# Revit family: QSTE
name_source: partatom
category: Mechanical Equipment
revit_build: Autodesk Revit 2018 (Build: 20170223_1515(x64)
units: mm (PartAtom-declared; Revit-internal decimal feet)

## family parameters
Always vertical = Yes
Cut with Voids When Loaded = No
OmniClass Number = 23.75.00.00
OmniClass Title = Climate Control (HVAC)
Part Type = Normal
Room Calculation Point = No
Round Connector Dimension = Use Diameter
Shared = No
Work Plane-Based = No

## types (56) — shared parameters
DUCT-FLANGE = 0' - 1"
Description = SERIES ELECTRIC HEAT
ESTH-depth = 0' - 8"
ESTH-flange = 0' - 0 3/4"
ESTH-offset = 0' - 6 1/2"
EnclHdim = 0' - 6 1/2"
EnclLdim = 1' - 10 1/4"
EnclOffset = 0' - 4 1/2"
EnclWdim = 0' - 11 1/8"
Inlet S = 0' - 5 1/2"
Inlet-offset = 0' - 4"
Manufacturer = ANEMOSTAT
Model = QSTE

## per-type parameters (varying)
- QSTE-1/4-HP-10L-S/ELBOW: BoX H=1' - 6"; Box H=1' - 6"; Box L=3' - 0"; Box W=2' - 8"; DUCT-C=1' - 0"; DUCT-D=1' - 4"; Discharge Height Y=0' - 11"; Discharge Width X=0' - 11 1/2"; Discharge for LH=Yes; Discharge for RH=No; ESTH for LH=Yes; ESTH for RH=No; ESTH-OAH=1' - 0 1/2"; ESTH-OAW=1' - 9 3/4"; Enclosure for LH=Yes; Enclosure for RH=No; Induction for LH=No; Induction for RH=No; Inlet Dia=0' - 9 7/8"; Inlet Radius=0' - 4 15/16"; Inlet for LH=Yes; Inlet for RH=No; Power Connect for LH=Yes; Power Connect for RH=No; Q5A=1' - 6"; Q5B=1' - 6"; Q5Q=1' - 6"; QSTE Discharge Offset=0' - 4 1/2"; Sound Elbow for LH=Yes; Sound Elbow for RH=No
- QSTE-1/2-HP-12L-S/ELBOW: BoX H=1' - 6"; Box H=1' - 6"; Box L=3' - 4"; Box W=3' - 4"; DUCT-C=1' - 5"; DUCT-D=1' - 4"; Discharge Height Y=1' - 0"; Discharge Width X=1' - 2"; Discharge for LH=Yes; Discharge for RH=No; ESTH for LH=Yes; ESTH for RH=No; ESTH-OAH=1' - 1 1/2"; ESTH-OAW=2' - 0 1/4"; Enclosure for LH=Yes; Enclosure for RH=No; Induction for LH=No; Induction for RH=No; Inlet Dia=0' - 11 7/8"; Inlet Radius=0' - 5 15/16"; Inlet for LH=Yes; Inlet for RH=No; Power Connect for LH=Yes; Power Connect for RH=No; Q5A=1' - 6"; Q5B=1' - 8"; Q5Q=1' - 6"; QSTE Discharge Offset=0' - 4 1/2"; Sound Elbow for LH=Yes; Sound Elbow for RH=No
- QSTE-1/2-HP-14L-S/ELBOW: BoX H=1' - 6"; Box H=1' - 6"; Box L=3' - 4"; Box W=3' - 4"; DUCT-C=1' - 5"; DUCT-D=1' - 4"; Discharge Height Y=1' - 0"; Discharge Width X=1' - 2"; Discharge for LH=Yes; Discharge for RH=No; ESTH for LH=Yes; ESTH for RH=No; ESTH-OAH=1' - 1 1/2"; ESTH-OAW=2' - 0 1/4"; Enclosure for LH=Yes; Enclosure for RH=No; Induction for LH=No; Induction for RH=No; Inlet Dia=1' - 1 7/8"; Inlet Radius=0' - 6 15/16"; Inlet for LH=Yes; Inlet for RH=No; Power Connect for LH=Yes; Power Connect for RH=No; Q5A=1' - 6"; Q5B=1' - 8"; Q5Q=1' - 6"; QSTE Discharge Offset=0' - 4 1/2"; Sound Elbow for LH=Yes; Sound Elbow for RH=No
- QSTE-3/4-HP-12L-S/ELBOW: BoX H=1' - 8"; Box H=1' - 8"; Box L=4' - 0"; Box W=4' - 0"; DUCT-C=1' - 9"; DUCT-D=1' - 6"; Discharge Height Y=1' - 4"; Discharge Width X=1' - 7"; Discharge for LH=Yes; Discharge for RH=No; ESTH for LH=Yes; ESTH for RH=No; ESTH-OAH=1' - 5 1/2"; ESTH-OAW=2' - 5 1/4"; Enclosure for LH=Yes; Enclosure for RH=No; Induction for LH=No; Induction for RH=No; Inlet Dia=0' - 11 7/8"; Inlet Radius=0' - 5 15/16"; Inlet for LH=Yes; Inlet for RH=No; Power Connect for LH=Yes; Power Connect for RH=No; Q5A=1' - 8"; Q5B=2' - 0"; Q5Q=1' - 8"; QSTE Discharge Offset=0' - 4 1/2"; Sound Elbow for LH=Yes; Sound Elbow for RH=No
- QSTE-3/4-HP-14L-S/ELBOW: BoX H=1' - 8"; Box H=1' - 8"; Box L=4' - 0"; Box W=4' - 0"; DUCT-C=1' - 9"; DUCT-D=1' - 6"; Discharge Height Y=1' - 4"; Discharge Width X=1' - 7"; Discharge for LH=Yes; Discharge for RH=No; ESTH for LH=Yes; ESTH for RH=No; ESTH-OAH=1' - 5 1/2"; ESTH-OAW=2' - 5 1/4"; Enclosure for LH=Yes; Enclosure for RH=No; Induction for LH=No; Induction for RH=No; Inlet Dia=1' - 1 7/8"; Inlet Radius=0' - 6 15/16"; Inlet for LH=Yes; Inlet for RH=No; Power Connect for LH=Yes; Power Connect for RH=No; Q5A=1' - 8"; Q5B=2' - 0"; Q5Q=1' - 8"; QSTE Discharge Offset=0' - 4 1/2"; Sound Elbow for LH=Yes; Sound Elbow for RH=No
- QSTE-1-HP-12L-S/ELBOW: BoX H=1' - 8"; Box H=1' - 8"; Box L=4' - 0"; Box W=4' - 0"; DUCT-C=1' - 9"; DUCT-D=1' - 6"; Discharge Height Y=1' - 4"; Discharge Width X=1' - 7"; Discharge for LH=Yes; Discharge for RH=No; ESTH for LH=Yes; ESTH for RH=No; ESTH-OAH=1' - 5 1/2"; ESTH-OAW=2' - 5 1/4"; Enclosure for LH=No; Enclosure for RH=Yes; Induction for LH=No; Induction for RH=No; Inlet Dia=0' - 11 7/8"; Inlet Radius=0' - 5 15/16"; Inlet for LH=Yes; Inlet for RH=No; Power Connect for LH=Yes; Power Connect for RH=No; Q5A=1' - 8"; Q5B=2' - 0"; Q5Q=1' - 8"; QSTE Discharge Offset=0' - 4 1/2"; Sound Elbow for LH=Yes; Sound Elbow for RH=No
- QSTE-1-HP-14L-W/OUT S/ELBOW: BoX H=1' - 8"; Box H=1' - 8"; Box L=4' - 0"; Box W=4' - 0"; DUCT-C=1' - 9"; DUCT-D=1' - 6"; Discharge Height Y=1' - 4"; Discharge Width X=1' - 7"; Discharge for LH=Yes; Discharge for RH=No; ESTH for LH=Yes; ESTH for RH=No; ESTH-OAH=1' - 5 1/2"; ESTH-OAW=2' - 5 1/4"; Enclosure for LH=Yes; Enclosure for RH=No; Induction for LH=Yes; Induction for RH=No; Inlet Dia=1' - 1 7/8"; Inlet Radius=0' - 6 15/16"; Inlet for LH=Yes; Inlet for RH=No; Power Connect for LH=Yes; Power Connect for RH=No; Q5A=1' - 8"; Q5B=2' - 0"; Q5Q=1' - 8"; QSTE Discharge Offset=0' - 4 1/2"; Sound Elbow for LH=No; Sound Elbow for RH=No
- QSTE-1-HP-16L-S/ELBOW: BoX H=1' - 8"; Box H=1' - 8"; Box L=4' - 0"; Box W=4' - 0"; DUCT-C=1' - 9"; DUCT-D=1' - 6"; Discharge Height Y=1' - 4"; Discharge Width X=1' - 7"; Discharge for LH=Yes; Discharge for RH=No; ESTH for LH=Yes; ESTH for RH=No; ESTH-OAH=1' - 5 1/2"; ESTH-OAW=2' - 5 1/4"; Enclosure for LH=Yes; Enclosure for RH=No; Induction for LH=No; Induction for RH=No; Inlet Dia=1' - 3 7/8"; Inlet Radius=0' - 7 15/16"; Inlet for LH=Yes; Inlet for RH=No; Power Connect for LH=Yes; Power Connect for RH=No; Q5A=1' - 8"; Q5B=2' - 0"; Q5Q=1' - 8"; QSTE Discharge Offset=0' - 4 1/2"; Sound Elbow for LH=Yes; Sound Elbow for RH=No
- QSTE-1/2-HP-10R-S/ELBOW: BoX H=1' - 6"; Box H=1' - 6"; Box L=3' - 4"; Box W=3' - 4"; DUCT-C=1' - 5"; DUCT-D=1' - 4"; Discharge Height Y=1' - 0"; Discharge Width X=1' - 2"; Discharge for LH=No; Discharge for RH=Yes; ESTH for LH=No; ESTH for RH=Yes; ESTH-OAH=1' - 1 1/2"; ESTH-OAW=2' - 0 1/4"; Enclosure for LH=No; Enclosure for RH=Yes; Induction for LH=No; Induction for RH=No; Inlet Dia=0' - 9 7/8"; Inlet Radius=0' - 4 15/16"; Inlet for LH=No; Inlet for RH=Yes; Power Connect for LH=No; Power Connect for RH=Yes; Q5A=1' - 6"; Q5B=1' - 8"; Q5Q=1' - 6"; QSTE Discharge Offset=0' - 4 1/2"; Sound Elbow for LH=No; Sound Elbow for RH=Yes
- QSTE-1/2-HP-12R-S/ELBOW: BoX H=1' - 6"; Box H=1' - 6"; Box L=3' - 4"; Box W=3' - 4"; DUCT-C=1' - 5"; DUCT-D=1' - 4"; Discharge Height Y=1' - 0"; Discharge Width X=1' - 2"; Discharge for LH=No; Discharge for RH=Yes; ESTH for LH=No; ESTH for RH=Yes; ESTH-OAH=1' - 1 1/2"; ESTH-OAW=2' - 0 1/4"; Enclosure for LH=No; Enclosure for RH=Yes; Induction for LH=No; Induction for RH=No; Inlet Dia=0' - 11 7/8"; Inlet Radius=0' - 5 15/16"; Inlet for LH=No; Inlet for RH=Yes; Power Connect for LH=No; Power Connect for RH=Yes; Q5A=1' - 6"; Q5B=1' - 8"; Q5Q=1' - 6"; QSTE Discharge Offset=0' - 4 1/2"; Sound Elbow for LH=No; Sound Elbow for RH=Yes
- QSTE-1/2-HP-14R-S/ELBOW: BoX H=1' - 6"; Box H=1' - 6"; Box L=3' - 4"; Box W=3' - 4"; DUCT-C=1' - 5"; DUCT-D=1' - 4"; Discharge Height Y=1' - 0"; Discharge Width X=1' - 2"; Discharge for LH=No; Discharge for RH=Yes; ESTH for LH=No; ESTH for RH=Yes; ESTH-OAH=1' - 1 1/2"; ESTH-OAW=2' - 0 1/4"; Enclosure for LH=No; Enclosure for RH=Yes; Induction for LH=No; Induction for RH=No; Inlet Dia=1' - 1 7/8"; Inlet Radius=0' - 6 15/16"; Inlet for LH=No; Inlet for RH=Yes; Power Connect for LH=No; Power Connect for RH=Yes; Q5A=1' - 6"; Q5B=1' - 8"; Q5Q=1' - 6"; QSTE Discharge Offset=0' - 4 1/2"; Sound Elbow for LH=No; Sound Elbow for RH=Yes
- QSTE-1/4-HP-10R-S/ELBOW: BoX H=1' - 6"; Box H=1' - 6"; Box L=3' - 0"; Box W=2' - 8"; DUCT-C=1' - 0"; DUCT-D=1' - 4"; Discharge Height Y=0' - 11"; Discharge Width X=0' - 11 1/2"; Discharge for LH=No; Discharge for RH=Yes; ESTH for LH=No; ESTH for RH=Yes; ESTH-OAH=1' - 0 1/2"; ESTH-OAW=1' - 9 3/4"; Enclosure for LH=No; Enclosure for RH=No; Induction for LH=No; Induction for RH=No; Inlet Dia=0' - 9 7/8"; Inlet Radius=0' - 4 15/16"; Inlet for LH=No; Inlet for RH=Yes; Power Connect for LH=No; Power Connect for RH=Yes; Q5A=1' - 6"; Q5B=1' - 6"; Q5Q=1' - 6"; QSTE Discharge Offset=0' - 4 1/2"; Sound Elbow for LH=No; Sound Elbow for RH=Yes
- QSTE-1-HP-12R-W/OUT S/ELBOW: BoX H=1' - 8"; Box H=1' - 8"; Box L=4' - 0"; Box W=4' - 0"; DUCT-C=1' - 9"; DUCT-D=1' - 6"; Discharge Height Y=1' - 4"; Discharge Width X=1' - 7"; Discharge for LH=No; Discharge for RH=Yes; ESTH for LH=No; ESTH for RH=Yes; ESTH-OAH=1' - 5 1/2"; ESTH-OAW=2' - 5 1/4"; Enclosure for LH=No; Enclosure for RH=Yes; Induction for LH=No; Induction for RH=Yes; Inlet Dia=0' - 11 7/8"; Inlet Radius=0' - 5 15/16"; Inlet for LH=No; Inlet for RH=Yes; Power Connect for LH=No; Power Connect for RH=Yes; Q5A=1' - 8"; Q5B=2' - 0"; Q5Q=1' - 8"; QSTE Discharge Offset=0' - 4 1/2"; Sound Elbow for LH=No; Sound Elbow for RH=No
- QSTE-1-HP-14R-S/ELBOW: BoX H=1' - 8"; Box H=1' - 8"; Box L=4' - 0"; Box W=4' - 0"; DUCT-C=1' - 9"; DUCT-D=1' - 6"; Discharge Height Y=1' - 4"; Discharge Width X=1' - 7"; Discharge for LH=No; Discharge for RH=Yes; ESTH for LH=No; ESTH for RH=Yes; ESTH-OAH=1' - 5 1/2"; ESTH-OAW=2' - 5 1/4"; Enclosure for LH=No; Enclosure for RH=Yes; Induction for LH=No; Induction for RH=No; Inlet Dia=1' - 1 7/8"; Inlet Radius=0' - 6 15/16"; Inlet for LH=No; Inlet for RH=Yes; Power Connect for LH=No; Power Connect for RH=Yes; Q5A=1' - 8"; Q5B=2' - 0"; Q5Q=1' - 8"; QSTE Discharge Offset=0' - 4 1/2"; Sound Elbow for LH=No; Sound Elbow for RH=Yes
- QSTE-1-HP-16R-S/ELBOW: BoX H=1' - 8"; Box H=1' - 8"; Box L=4' - 0"; Box W=4' - 0"; DUCT-C=1' - 9"; DUCT-D=1' - 6"; Discharge Height Y=1' - 4"; Discharge Width X=1' - 7"; Discharge for LH=No; Discharge for RH=Yes; ESTH for LH=No; ESTH for RH=Yes; ESTH-OAH=1' - 5 1/2"; ESTH-OAW=2' - 5 1/4"; Enclosure for LH=No; Enclosure for RH=Yes; Induction for LH=No; Induction for RH=No; Inlet Dia=1' - 3 7/8"; Inlet Radius=0' - 7 15/16"; Inlet for LH=No; Inlet for RH=Yes; Power Connect for LH=No; Power Connect for RH=Yes; Q5A=1' - 8"; Q5B=2' - 0"; Q5Q=1' - 8"; QSTE Discharge Offset=0' - 4 1/2"; Sound Elbow for LH=No; Sound Elbow for RH=Yes
- QSTE-3/4-HP-12R-S/ELBOW: BoX H=1' - 8"; Box H=1' - 8"; Box L=4' - 0"; Box W=4' - 0"; DUCT-C=1' - 9"; DUCT-D=1' - 6"; Discharge Height Y=1' - 4"; Discharge Width X=1' - 7"; Discharge for LH=No; Discharge for RH=Yes; ESTH for LH=No; ESTH for RH=Yes; ESTH-OAH=1' - 5 1/2"; ESTH-OAW=2' - 5 1/4"; Enclosure for LH=No; Enclosure for RH=Yes; Induction for LH=No; Induction for RH=No; Inlet Dia=0' - 11 7/8"; Inlet Radius=0' - 5 15/16"; Inlet for LH=No; Inlet for RH=Yes; Power Connect for LH=No; Power Connect for RH=Yes; Q5A=1' - 8"; Q5B=2' - 0"; Q5Q=1' - 8"; QSTE Discharge Offset=0' - 4 1/2"; Sound Elbow for LH=No; Sound Elbow for RH=Yes
- QSTE-3/4-HP-14R-S/ELBOW: BoX H=1' - 8"; Box H=1' - 8"; Box L=4' - 0"; Box W=4' - 0"; DUCT-C=1' - 9"; DUCT-D=1' - 6"; Discharge Height Y=1' - 4"; Discharge Width X=1' - 7"; Discharge for LH=No; Discharge for RH=Yes; ESTH for LH=No; ESTH for RH=Yes; ESTH-OAH=1' - 5 1/2"; ESTH-OAW=2' - 5 1/4"; Enclosure for LH=No; Enclosure for RH=Yes; Induction for LH=No; Induction for RH=No; Inlet Dia=1' - 1 7/8"; Inlet Radius=0' - 6 15/16"; Inlet for LH=No; Inlet for RH=Yes; Power Connect for LH=No; Power Connect for RH=Yes; Q5A=1' - 8"; Q5B=2' - 0"; Q5Q=1' - 8"; QSTE Discharge Offset=0' - 4 1/2"; Sound Elbow for LH=No; Sound Elbow for RH=Yes
- QSTE-1/2-HP-10L-W/OUT S/ELBOW: BoX H=1' - 6"; Box H=1' - 6"; Box L=3' - 4"; Box W=3' - 4"; DUCT-C=1' - 5"; DUCT-D=1' - 4"; Discharge Height Y=1' - 0"; Discharge Width X=1' - 2"; Discharge for LH=Yes; Discharge for RH=No; ESTH for LH=Yes; ESTH for RH=No; ESTH-OAH=1' - 1 1/2"; ESTH-OAW=2' - 0 1/4"; Enclosure for LH=Yes; Enclosure for RH=No; Induction for LH=Yes; Induction for RH=No; Inlet Dia=0' - 9 7/8"; Inlet Radius=0' - 4 15/16"; Inlet for LH=Yes; Inlet for RH=No; Power Connect for LH=Yes; Power Connect for RH=No; Q5A=1' - 6"; Q5B=1' - 8"; Q5Q=1' - 6"; QSTE Discharge Offset=0' - 4 1/2"; Sound Elbow for LH=No; Sound Elbow for RH=No
- QSTE-1/2-HP-10R-W/OUT S/ELBOW: BoX H=1' - 6"; Box H=1' - 6"; Box L=3' - 4"; Box W=3' - 4"; DUCT-C=1' - 5"; DUCT-D=1' - 4"; Discharge Height Y=1' - 0"; Discharge Width X=1' - 2"; Discharge for LH=No; Discharge for RH=Yes; ESTH for LH=No; ESTH for RH=Yes; ESTH-OAH=1' - 1 1/2"; ESTH-OAW=2' - 0 1/4"; Enclosure for LH=No; Enclosure for RH=Yes; Induction for LH=No; Induction for RH=Yes; Inlet Dia=0' - 9 7/8"; Inlet Radius=0' - 4 15/16"; Inlet for LH=No; Inlet for RH=Yes; Power Connect for LH=No; Power Connect for RH=Yes; Q5A=1' - 6"; Q5B=1' - 8"; Q5Q=1' - 6"; QSTE Discharge Offset=0' - 4 1/2"; Sound Elbow for LH=No; Sound Elbow for RH=No
- QSTE-1/2-HP-12L-W/OUT S/ELBOW: BoX H=1' - 6"; Box H=1' - 6"; Box L=3' - 4"; Box W=3' - 4"; DUCT-C=1' - 5"; DUCT-D=1' - 4"; Discharge Height Y=1' - 0"; Discharge Width X=1' - 2"; Discharge for LH=Yes; Discharge for RH=No; ESTH for LH=Yes; ESTH for RH=No; ESTH-OAH=1' - 1 1/2"; ESTH-OAW=2' - 0 1/4"; Enclosure for LH=Yes; Enclosure for RH=No; Induction for LH=Yes; Induction for RH=No; Inlet Dia=0' - 11 7/8"; Inlet Radius=0' - 5 15/16"; Inlet for LH=Yes; Inlet for RH=No; Power Connect for LH=Yes; Power Connect for RH=No; Q5A=1' - 6"; Q5B=1' - 8"; Q5Q=1' - 6"; QSTE Discharge Offset=0' - 4 1/2"; Sound Elbow for LH=No; Sound Elbow for RH=No
- QSTE-1/2-HP-12R-W/OUT S/ELBOW: BoX H=1' - 6"; Box H=1' - 6"; Box L=3' - 4"; Box W=3' - 4"; DUCT-C=1' - 5"; DUCT-D=1' - 4"; Discharge Height Y=1' - 0"; Discharge Width X=1' - 2"; Discharge for LH=No; Discharge for RH=Yes; ESTH for LH=No; ESTH for RH=Yes; ESTH-OAH=1' - 1 1/2"; ESTH-OAW=2' - 0 1/4"; Enclosure for LH=No; Enclosure for RH=Yes; Induction for LH=No; Induction for RH=Yes; Inlet Dia=0' - 11 7/8"; Inlet Radius=0' - 5 15/16"; Inlet for LH=No; Inlet for RH=Yes; Power Connect for LH=No; Power Connect for RH=Yes; Q5A=1' - 6"; Q5B=1' - 8"; Q5Q=1' - 6"; QSTE Discharge Offset=0' - 4 1/2"; Sound Elbow for LH=No; Sound Elbow for RH=No
- QSTE-1/2-HP-14L-W/OUT S/ELBOW: BoX H=1' - 6"; Box H=1' - 6"; Box L=3' - 4"; Box W=3' - 4"; DUCT-C=1' - 5"; DUCT-D=1' - 4"; Discharge Height Y=1' - 0"; Discharge Width X=1' - 2"; Discharge for LH=Yes; Discharge for RH=No; ESTH for LH=Yes; ESTH for RH=No; ESTH-OAH=1' - 1 1/2"; ESTH-OAW=2' - 0 1/4"; Enclosure for LH=Yes; Enclosure for RH=No; Induction for LH=Yes; Induction for RH=No; Inlet Dia=1' - 1 7/8"; Inlet Radius=0' - 6 15/16"; Inlet for LH=Yes; Inlet for RH=No; Power Connect for LH=Yes; Power Connect for RH=No; Q5A=1' - 6"; Q5B=1' - 8"; Q5Q=1' - 6"; QSTE Discharge Offset=0' - 4 1/2"; Sound Elbow for LH=No; Sound Elbow for RH=No
- QSTE-1/2-HP-14R-W/OUT S/ELBOW: BoX H=1' - 6"; Box H=1' - 6"; Box L=3' - 4"; Box W=3' - 4"; DUCT-C=1' - 5"; DUCT-D=1' - 4"; Discharge Height Y=1' - 0"; Discharge Width X=1' - 2"; Discharge for LH=No; Discharge for RH=Yes; ESTH for LH=No; ESTH for RH=Yes; ESTH-OAH=1' - 1 1/2"; ESTH-OAW=2' - 0 1/4"; Enclosure for LH=No; Enclosure for RH=Yes; Induction for LH=No; Induction for RH=Yes; Inlet Dia=1' - 1 7/8"; Inlet Radius=0' - 6 15/16"; Inlet for LH=No; Inlet for RH=Yes; Power Connect for LH=No; Power Connect for RH=Yes; Q5A=1' - 6"; Q5B=1' - 8"; Q5Q=1' - 6"; QSTE Discharge Offset=0' - 4 1/2"; Sound Elbow for LH=No; Sound Elbow for RH=No
- QSTE-1/6-HP-6R-W/OUT S/ELBOW: BoX H=1' - 6"; Box H=1' - 6"; Box L=3' - 0"; Box W=2' - 8"; DUCT-C=1' - 5"; DUCT-D=1' - 4"; Discharge Height Y=0' - 11"; Discharge Width X=0' - 11 1/2"; Discharge for LH=No; Discharge for RH=Yes; ESTH for LH=No; ESTH for RH=Yes; ESTH-OAH=1' - 0 1/2"; ESTH-OAW=1' - 9 3/4"; Enclosure for LH=No; Enclosure for RH=Yes; Induction for LH=No; Induction for RH=Yes; Inlet Dia=0' - 5 7/8"; Inlet Radius=0' - 2 15/16"; Inlet for LH=No; Inlet for RH=Yes; Power Connect for LH=No; Power Connect for RH=Yes; Q5A=1' - 6"; Q5B=1' - 6"; Q5Q=1' - 6"; QSTE Discharge Offset=0' - 4 1/2"; Sound Elbow for LH=No; Sound Elbow for RH=No
- QSTE-1/6-HP-7R-W/OUT S/ELBOW: BoX H=1' - 6"; Box H=1' - 6"; Box L=3' - 0"; Box W=2' - 8"; DUCT-C=1' - 0"; DUCT-D=1' - 4"; Discharge Height Y=0' - 11"; Discharge Width X=0' - 11 1/2"; Discharge for LH=No; Discharge for RH=Yes; ESTH for LH=No; ESTH for RH=Yes; ESTH-OAH=1' - 0 1/2"; ESTH-OAW=1' - 9 3/4"; Enclosure for LH=No; Enclosure for RH=Yes; Induction for LH=No; Induction for RH=Yes; Inlet Dia=0' - 6 7/8"; Inlet Radius=0' - 3 7/16"; Inlet for LH=No; Inlet for RH=Yes; Power Connect for LH=No; Power Connect for RH=Yes; Q5A=1' - 6"; Q5B=1' - 6"; Q5Q=1' - 6"; QSTE Discharge Offset=0' - 4 1/2"; Sound Elbow for LH=No; Sound Elbow for RH=No
- QSTE-1/6-HP-8R-W/OUT S/ELBOW: BoX H=1' - 6"; Box H=1' - 6"; Box L=3' - 0"; Box W=2' - 8"; DUCT-C=1' - 0"; DUCT-D=1' - 4"; Discharge Height Y=0' - 11"; Discharge Width X=0' - 11 1/2"; Discharge for LH=No; Discharge for RH=Yes; ESTH for LH=No; ESTH for RH=Yes; ESTH-OAH=1' - 0 1/2"; ESTH-OAW=1' - 9 3/4"; Enclosure for LH=No; Enclosure for RH=Yes; Induction for LH=No; Induction for RH=Yes; Inlet Dia=0' - 7 7/8"; Inlet Radius=0' - 3 15/16"; Inlet for LH=No; Inlet for RH=Yes; Power Connect for LH=No; Power Connect for RH=Yes; Q5A=1' - 6"; Q5B=1' - 6"; Q5Q=1' - 6"; QSTE Discharge Offset=0' - 4 1/2"; Sound Elbow for LH=No; Sound Elbow for RH=No
- QSTE-1/6-HP-8L-W/OUT S/ELBOW: BoX H=1' - 6"; Box H=1' - 6"; Box L=3' - 0"; Box W=2' - 8"; DUCT-C=1' - 0"; DUCT-D=1' - 4"; Discharge Height Y=0' - 11"; Discharge Width X=0' - 11 1/2"; Discharge for LH=Yes; Discharge for RH=No; ESTH for LH=Yes; ESTH for RH=No; ESTH-OAH=1' - 0 1/2"; ESTH-OAW=1' - 9 3/4"; Enclosure for LH=Yes; Enclosure for RH=No; Induction for LH=Yes; Induction for RH=No; Inlet Dia=0' - 7 7/8"; Inlet Radius=0' - 3 15/16"; Inlet for LH=Yes; Inlet for RH=No; Power Connect for LH=Yes; Power Connect for RH=No; Q5A=1' - 6"; Q5B=1' - 6"; Q5Q=1' - 6"; QSTE Discharge Offset=0' - 4 1/2"; Sound Elbow for LH=No; Sound Elbow for RH=No
- QSTE-1/4-HP-9L-W/OUT S/ELBOW: BoX H=1' - 6"; Box H=1' - 6"; Box L=3' - 0"; Box W=2' - 8"; DUCT-C=1' - 0"; DUCT-D=1' - 4"; Discharge Height Y=0' - 11"; Discharge Width X=0' - 11 1/2"; Discharge for LH=Yes; Discharge for RH=No; ESTH for LH=Yes; ESTH for RH=No; ESTH-OAH=1' - 0 1/2"; ESTH-OAW=1' - 9 3/4"; Enclosure for LH=Yes; Enclosure for RH=No; Induction for LH=Yes; Induction for RH=No; Inlet Dia=0' - 8 7/8"; Inlet Radius=0' - 4 7/16"; Inlet for LH=Yes; Inlet for RH=No; Power Connect for LH=Yes; Power Connect for RH=No; Q5A=1' - 6"; Q5B=1' - 6"; Q5Q=1' - 6"; QSTE Discharge Offset=0' - 4 1/2"; Sound Elbow for LH=No; Sound Elbow for RH=No
- QSTE-1/4-HP-9R-W/OUT S/ELBOW: BoX H=1' - 6"; Box H=1' - 6"; Box L=3' - 0"; Box W=2' - 8"; DUCT-C=1' - 0"; DUCT-D=1' - 4"; Discharge Height Y=0' - 11"; Discharge Width X=0' - 11 1/2"; Discharge for LH=No; Discharge for RH=Yes; ESTH for LH=No; ESTH for RH=Yes; ESTH-OAH=1' - 0 1/2"; ESTH-OAW=1' - 9 3/4"; Enclosure for LH=No; Enclosure for RH=Yes; Induction for LH=No; Induction for RH=Yes; Inlet Dia=0' - 8 7/8"; Inlet Radius=0' - 4 7/16"; Inlet for LH=No; Inlet for RH=Yes; Power Connect for LH=No; Power Connect for RH=Yes; Q5A=1' - 6"; Q5B=1' - 6"; Q5Q=1' - 6"; QSTE Discharge Offset=0' - 4 1/2"; Sound Elbow for LH=No; Sound Elbow for RH=No
- QSTE-1/4-HP-10L-W/OUT S/ELBOW: BoX H=1' - 6"; Box H=1' - 6"; Box L=3' - 0"; Box W=2' - 8"; DUCT-C=1' - 0"; DUCT-D=1' - 4"; Discharge Height Y=0' - 11"; Discharge Width X=0' - 11 1/2"; Discharge for LH=Yes; Discharge for RH=No; ESTH for LH=Yes; ESTH for RH=No; ESTH-OAH=1' - 0 1/2"; ESTH-OAW=1' - 9 3/4"; Enclosure for LH=Yes; Enclosure for RH=No; Induction for LH=Yes; Induction for RH=No; Inlet Dia=0' - 9 7/8"; Inlet Radius=0' - 4 15/16"; Inlet for LH=Yes; Inlet for RH=No; Power Connect for LH=Yes; Power Connect for RH=No; Q5A=1' - 6"; Q5B=1' - 6"; Q5Q=1' - 6"; QSTE Discharge Offset=0' - 4 1/2"; Sound Elbow for LH=No; Sound Elbow for RH=No
- QSTE-1/4-HP-10R-W/OUT S/ELBOW: BoX H=1' - 6"; Box H=1' - 6"; Box L=3' - 0"; Box W=2' - 8"; DUCT-C=1' - 0"; DUCT-D=1' - 4"; Discharge Height Y=0' - 11"; Discharge Width X=0' - 11 1/2"; Discharge for LH=No; Discharge for RH=Yes; ESTH for LH=No; ESTH for RH=Yes; ESTH-OAH=1' - 0 1/2"; ESTH-OAW=1' - 9 3/4"; Enclosure for LH=No; Enclosure for RH=Yes; Induction for LH=No; Induction for RH=Yes; Inlet Dia=0' - 9 7/8"; Inlet Radius=0' - 4 15/16"; Inlet for LH=No; Inlet for RH=Yes; Power Connect for LH=No; Power Connect for RH=Yes; Q5A=1' - 6"; Q5B=1' - 6"; Q5Q=1' - 6"; QSTE Discharge Offset=0' - 3"; Sound Elbow for LH=No; Sound Elbow for RH=No
- QSTE-1/6-HP-6L-W/OUT S/ELBOW: BoX H=1' - 6"; Box H=1' - 6"; Box L=3' - 0"; Box W=2' - 8"; DUCT-C=1' - 5"; DUCT-D=1' - 4"; Discharge Height Y=0' - 11"; Discharge Width X=0' - 11 1/2"; Discharge for LH=Yes; Discharge for RH=No; ESTH for LH=Yes; ESTH for RH=No; ESTH-OAH=1' - 0 1/2"; ESTH-OAW=1' - 9 3/4"; Enclosure for LH=Yes; Enclosure for RH=No; Induction for LH=Yes; Induction for RH=No; Inlet Dia=0' - 5 7/8"; Inlet Radius=0' - 2 15/16"; Inlet for LH=Yes; Inlet for RH=No; Power Connect for LH=Yes; Power Connect for RH=No; Q5A=1' - 6"; Q5B=1' - 6"; Q5Q=1' - 6"; QSTE Discharge Offset=0' - 4 1/2"; Sound Elbow for LH=No; Sound Elbow for RH=No
- QSTE-1/6-HP-6L-S/ELBOW: BoX H=1' - 6"; Box H=1' - 6"; Box L=3' - 0"; Box W=2' - 8"; DUCT-C=1' - 5"; DUCT-D=1' - 4"; Discharge Height Y=0' - 11"; Discharge Width X=0' - 11 1/2"; Discharge for LH=Yes; Discharge for RH=No; ESTH for LH=Yes; ESTH for RH=No; ESTH-OAH=1' - 0 1/2"; ESTH-OAW=1' - 9 3/4"; Enclosure for LH=Yes; Enclosure for RH=No; Induction for LH=No; Induction for RH=No; Inlet Dia=0' - 5 7/8"; Inlet Radius=0' - 2 15/16"; Inlet for LH=Yes; Inlet for RH=No; Power Connect for LH=Yes; Power Connect for RH=No; Q5A=1' - 6"; Q5B=1' - 6"; Q5Q=1' - 6"; QSTE Discharge Offset=0' - 4 1/2"; Sound Elbow for LH=Yes; Sound Elbow for RH=No
- QSTE-1/6-HP-6R-S/ELBOW: BoX H=1' - 6"; Box H=1' - 6"; Box L=3' - 0"; Box W=2' - 8"; DUCT-C=1' - 5"; DUCT-D=1' - 4"; Discharge Height Y=0' - 11"; Discharge Width X=0' - 11 1/2"; Discharge for LH=No; Discharge for RH=Yes; ESTH for LH=No; ESTH for RH=Yes; ESTH-OAH=1' - 0 1/2"; ESTH-OAW=1' - 9 3/4"; Enclosure for LH=No; Enclosure for RH=Yes; Induction for LH=No; Induction for RH=No; Inlet Dia=0' - 5 7/8"; Inlet Radius=0' - 2 15/16"; Inlet for LH=No; Inlet for RH=Yes; Power Connect for LH=No; Power Connect for RH=Yes; Q5A=1' - 6"; Q5B=1' - 6"; Q5Q=1' - 6"; QSTE Discharge Offset=0' - 4 1/2"; Sound Elbow for LH=No; Sound Elbow for RH=Yes
- QSTE-1/6-HP-7R-S/ELBOW: BoX H=1' - 6"; Box H=1' - 6"; Box L=3' - 0"; Box W=2' - 8"; DUCT-C=1' - 0"; DUCT-D=1' - 4"; Discharge Height Y=0' - 11"; Discharge Width X=0' - 11 1/2"; Discharge for LH=No; Discharge for RH=Yes; ESTH for LH=No; ESTH for RH=Yes; ESTH-OAH=1' - 0 1/2"; ESTH-OAW=1' - 9 3/4"; Enclosure for LH=No; Enclosure for RH=Yes; Induction for LH=No; Induction for RH=No; Inlet Dia=0' - 6 7/8"; Inlet Radius=0' - 3 7/16"; Inlet for LH=No; Inlet for RH=Yes; Power Connect for LH=No; Power Connect for RH=Yes; Q5A=1' - 6"; Q5B=1' - 6"; Q5Q=1' - 6"; QSTE Discharge Offset=0' - 4 1/2"; Sound Elbow for LH=No; Sound Elbow for RH=Yes
- QSTE-1/6-HP-7L-S/ELBOW: BoX H=1' - 6"; Box H=1' - 6"; Box L=3' - 0"; Box W=2' - 8"; DUCT-C=1' - 0"; DUCT-D=1' - 4"; Discharge Height Y=0' - 11"; Discharge Width X=0' - 11 1/2"; Discharge for LH=Yes; Discharge for RH=No; ESTH for LH=Yes; ESTH for RH=No; ESTH-OAH=1' - 0 1/2"; ESTH-OAW=1' - 9 3/4"; Enclosure for LH=Yes; Enclosure for RH=No; Induction for LH=No; Induction for RH=No; Inlet Dia=0' - 6 7/8"; Inlet Radius=0' - 3 7/16"; Inlet for LH=Yes; Inlet for RH=No; Power Connect for LH=Yes; Power Connect for RH=No; Q5A=1' - 6"; Q5B=1' - 6"; Q5Q=1' - 6"; QSTE Discharge Offset=0' - 4 1/2"; Sound Elbow for LH=Yes; Sound Elbow for RH=No
- QSTE-1/6-HP-7L-W/OUT S/ELBOW: BoX H=1' - 6"; Box H=1' - 6"; Box L=3' - 0"; Box W=2' - 8"; DUCT-C=1' - 0"; DUCT-D=1' - 4"; Discharge Height Y=0' - 11"; Discharge Width X=0' - 11 1/2"; Discharge for LH=Yes; Discharge for RH=No; ESTH for LH=Yes; ESTH for RH=No; ESTH-OAH=1' - 0 1/2"; ESTH-OAW=1' - 9 3/4"; Enclosure for LH=Yes; Enclosure for RH=No; Induction for LH=Yes; Induction for RH=No; Inlet Dia=0' - 6 7/8"; Inlet Radius=0' - 3 7/16"; Inlet for LH=Yes; Inlet for RH=No; Power Connect for LH=Yes; Power Connect for RH=No; Q5A=1' - 6"; Q5B=1' - 6"; Q5Q=1' - 6"; QSTE Discharge Offset=0' - 4 1/2"; Sound Elbow for LH=No; Sound Elbow for RH=No
- QSTE-1/4-HP-8L-S/ELBOW: BoX H=1' - 6"; Box H=1' - 6"; Box L=3' - 0"; Box W=2' - 8"; DUCT-C=1' - 0"; DUCT-D=1' - 4"; Discharge Height Y=0' - 11"; Discharge Width X=0' - 11 1/2"; Discharge for LH=Yes; Discharge for RH=No; ESTH for LH=Yes; ESTH for RH=No; ESTH-OAH=1' - 0 1/2"; ESTH-OAW=1' - 9 3/4"; Enclosure for LH=Yes; Enclosure for RH=No; Induction for LH=No; Induction for RH=No; Inlet Dia=0' - 7 7/8"; Inlet Radius=0' - 3 15/16"; Inlet for LH=Yes; Inlet for RH=No; Power Connect for LH=Yes; Power Connect for RH=No; Q5A=1' - 6"; Q5B=1' - 6"; Q5Q=1' - 6"; QSTE Discharge Offset=0' - 4 1/2"; Sound Elbow for LH=Yes; Sound Elbow for RH=No
- QSTE-1/6-HP-8R-S/ELBOW: BoX H=1' - 6"; Box H=1' - 6"; Box L=3' - 0"; Box W=2' - 8"; DUCT-C=1' - 0"; DUCT-D=1' - 4"; Discharge Height Y=0' - 11"; Discharge Width X=0' - 11 1/2"; Discharge for LH=No; Discharge for RH=Yes; ESTH for LH=No; ESTH for RH=Yes; ESTH-OAH=1' - 0 1/2"; ESTH-OAW=1' - 9 3/4"; Enclosure for LH=No; Enclosure for RH=Yes; Induction for LH=No; Induction for RH=No; Inlet Dia=0' - 7 7/8"; Inlet Radius=0' - 3 15/16"; Inlet for LH=No; Inlet for RH=Yes; Power Connect for LH=No; Power Connect for RH=Yes; Q5A=1' - 6"; Q5B=1' - 6"; Q5Q=1' - 6"; QSTE Discharge Offset=0' - 4 1/2"; Sound Elbow for LH=No; Sound Elbow for RH=Yes
- QSTE-1/4-HP-9L-S/ELBOW: BoX H=1' - 6"; Box H=1' - 6"; Box L=3' - 0"; Box W=2' - 8"; DUCT-C=1' - 0"; DUCT-D=1' - 4"; Discharge Height Y=0' - 11"; Discharge Width X=0' - 11 1/2"; Discharge for LH=Yes; Discharge for RH=No; ESTH for LH=Yes; ESTH for RH=No; ESTH-OAH=1' - 0 1/2"; ESTH-OAW=1' - 9 3/4"; Enclosure for LH=Yes; Enclosure for RH=No; Induction for LH=No; Induction for RH=No; Inlet Dia=0' - 8 7/8"; Inlet Radius=0' - 4 7/16"; Inlet for LH=Yes; Inlet for RH=No; Power Connect for LH=Yes; Power Connect for RH=No; Q5A=1' - 6"; Q5B=1' - 6"; Q5Q=1' - 6"; QSTE Discharge Offset=0' - 4 1/2"; Sound Elbow for LH=Yes; Sound Elbow for RH=No
- QSTE-1/4-HP-9R-S/ELBOW: BoX H=1' - 6"; Box H=1' - 6"; Box L=3' - 0"; Box W=2' - 8"; DUCT-C=1' - 0"; DUCT-D=1' - 4"; Discharge Height Y=0' - 11"; Discharge Width X=0' - 11 1/2"; Discharge for LH=No; Discharge for RH=Yes; ESTH for LH=No; ESTH for RH=Yes; ESTH-OAH=1' - 0 1/2"; ESTH-OAW=1' - 9 3/4"; Enclosure for LH=No; Enclosure for RH=Yes; Induction for LH=No; Induction for RH=No; Inlet Dia=0' - 8 7/8"; Inlet Radius=0' - 4 7/16"; Inlet for LH=No; Inlet for RH=Yes; Power Connect for LH=No; Power Connect for RH=Yes; Q5A=1' - 6"; Q5B=1' - 6"; Q5Q=1' - 6"; QSTE Discharge Offset=0' - 4 1/2"; Sound Elbow for LH=No; Sound Elbow for RH=Yes
- QSTE-1-HP-12L-W/OUT S/ELBOW: BoX H=1' - 8"; Box H=1' - 8"; Box L=4' - 0"; Box W=4' - 0"; DUCT-C=1' - 9"; DUCT-D=1' - 6"; Discharge Height Y=1' - 4"; Discharge Width X=1' - 7"; Discharge for LH=Yes; Discharge for RH=No; ESTH for LH=Yes; ESTH for RH=No; ESTH-OAH=1' - 5 1/2"; ESTH-OAW=2' - 5 1/4"; Enclosure for LH=No; Enclosure for RH=Yes; Induction for LH=Yes; Induction for RH=No; Inlet Dia=0' - 11 7/8"; Inlet Radius=0' - 5 15/16"; Inlet for LH=Yes; Inlet for RH=No; Power Connect for LH=Yes; Power Connect for RH=No; Q5A=1' - 8"; Q5B=2' - 0"; Q5Q=1' - 8"; QSTE Discharge Offset=0' - 4 1/2"; Sound Elbow for LH=No; Sound Elbow for RH=No
- QSTE-1-HP-12R-S/ELBOW: BoX H=1' - 8"; Box H=1' - 8"; Box L=4' - 0"; Box W=4' - 0"; DUCT-C=1' - 9"; DUCT-D=1' - 6"; Discharge Height Y=1' - 4"; Discharge Width X=1' - 7"; Discharge for LH=No; Discharge for RH=Yes; ESTH for LH=No; ESTH for RH=Yes; ESTH-OAH=1' - 5 1/2"; ESTH-OAW=2' - 5 1/4"; Enclosure for LH=No; Enclosure for RH=Yes; Induction for LH=No; Induction for RH=No; Inlet Dia=0' - 11 7/8"; Inlet Radius=0' - 5 15/16"; Inlet for LH=No; Inlet for RH=Yes; Power Connect for LH=No; Power Connect for RH=Yes; Q5A=1' - 8"; Q5B=2' - 0"; Q5Q=1' - 8"; QSTE Discharge Offset=0' - 4 1/2"; Sound Elbow for LH=No; Sound Elbow for RH=Yes
- QSTE-1-HP-14L-S/ELBOW: BoX H=1' - 8"; Box H=1' - 8"; Box L=4' - 0"; Box W=4' - 0"; DUCT-C=1' - 9"; DUCT-D=1' - 6"; Discharge Height Y=1' - 4"; Discharge Width X=1' - 7"; Discharge for LH=Yes; Discharge for RH=No; ESTH for LH=Yes; ESTH for RH=No; ESTH-OAH=1' - 5 1/2"; ESTH-OAW=2' - 5 1/4"; Enclosure for LH=Yes; Enclosure for RH=No; Induction for LH=No; Induction for RH=No; Inlet Dia=1' - 1 7/8"; Inlet Radius=0' - 6 15/16"; Inlet for LH=Yes; Inlet for RH=No; Power Connect for LH=Yes; Power Connect for RH=No; Q5A=1' - 8"; Q5B=2' - 0"; Q5Q=1' - 8"; QSTE Discharge Offset=0' - 4 1/2"; Sound Elbow for LH=Yes; Sound Elbow for RH=No
- QSTE-1-HP-14R-W/OUT S/ELBOW: BoX H=1' - 8"; Box H=1' - 8"; Box L=4' - 0"; Box W=4' - 0"; DUCT-C=1' - 9"; DUCT-D=1' - 6"; Discharge Height Y=1' - 4"; Discharge Width X=1' - 7"; Discharge for LH=No; Discharge for RH=Yes; ESTH for LH=No; ESTH for RH=Yes; ESTH-OAH=1' - 5 1/2"; ESTH-OAW=2' - 5 1/4"; Enclosure for LH=No; Enclosure for RH=Yes; Induction for LH=No; Induction for RH=Yes; Inlet Dia=1' - 1 7/8"; Inlet Radius=0' - 6 15/16"; Inlet for LH=No; Inlet for RH=Yes; Power Connect for LH=No; Power Connect for RH=Yes; Q5A=1' - 8"; Q5B=2' - 0"; Q5Q=1' - 8"; QSTE Discharge Offset=0' - 4 1/2"; Sound Elbow for LH=No; Sound Elbow for RH=No
- QSTE-1-HP-16L-W/OUT S/ELBOW: BoX H=1' - 8"; Box H=1' - 8"; Box L=4' - 0"; Box W=4' - 0"; DUCT-C=1' - 9"; DUCT-D=1' - 6"; Discharge Height Y=1' - 4"; Discharge Width X=1' - 7"; Discharge for LH=Yes; Discharge for RH=No; ESTH for LH=Yes; ESTH for RH=No; ESTH-OAH=1' - 5 1/2"; ESTH-OAW=2' - 5 1/4"; Enclosure for LH=Yes; Enclosure for RH=No; Induction for LH=Yes; Induction for RH=No; Inlet Dia=1' - 3 7/8"; Inlet Radius=0' - 7 15/16"; Inlet for LH=Yes; Inlet for RH=No; Power Connect for LH=Yes; Power Connect for RH=No; Q5A=1' - 8"; Q5B=2' - 0"; Q5Q=1' - 8"; QSTE Discharge Offset=0' - 4 1/2"; Sound Elbow for LH=No; Sound Elbow for RH=No
- QSTE-1-HP-16R-W/OUT S/ELBOW: BoX H=1' - 8"; Box H=1' - 8"; Box L=4' - 0"; Box W=4' - 0"; DUCT-C=1' - 9"; DUCT-D=1' - 6"; Discharge Height Y=1' - 4"; Discharge Width X=1' - 7"; Discharge for LH=No; Discharge for RH=Yes; ESTH for LH=No; ESTH for RH=Yes; ESTH-OAH=1' - 5 1/2"; ESTH-OAW=2' - 5 1/4"; Enclosure for LH=No; Enclosure for RH=Yes; Induction for LH=No; Induction for RH=Yes; Inlet Dia=1' - 3 7/8"; Inlet Radius=0' - 7 15/16"; Inlet for LH=No; Inlet for RH=Yes; Power Connect for LH=No; Power Connect for RH=Yes; Q5A=1' - 8"; Q5B=2' - 0"; Q5Q=1' - 8"; QSTE Discharge Offset=0' - 4 1/2"; Sound Elbow for LH=No; Sound Elbow for RH=No
- QSTE-3/4-HP-12L-W/OUT S/ELBOW: BoX H=1' - 8"; Box H=1' - 8"; Box L=4' - 0"; Box W=4' - 0"; DUCT-C=1' - 9"; DUCT-D=1' - 6"; Discharge Height Y=1' - 4"; Discharge Width X=1' - 7"; Discharge for LH=Yes; Discharge for RH=No; ESTH for LH=Yes; ESTH for RH=No; ESTH-OAH=1' - 5 1/2"; ESTH-OAW=2' - 5 1/4"; Enclosure for LH=Yes; Enclosure for RH=No; Induction for LH=Yes; Induction for RH=No; Inlet Dia=0' - 11 7/8"; Inlet Radius=0' - 5 15/16"; Inlet for LH=Yes; Inlet for RH=No; Power Connect for LH=Yes; Power Connect for RH=No; Q5A=1' - 8"; Q5B=2' - 0"; Q5Q=1' - 8"; QSTE Discharge Offset=0' - 4 1/2"; Sound Elbow for LH=No; Sound Elbow for RH=No
- QSTE-3/4-HP-12R-W/OUT S/ELBOW: BoX H=1' - 8"; Box H=1' - 8"; Box L=4' - 0"; Box W=4' - 0"; DUCT-C=1' - 9"; DUCT-D=1' - 6"; Discharge Height Y=1' - 4"; Discharge Width X=1' - 7"; Discharge for LH=No; Discharge for RH=Yes; ESTH for LH=No; ESTH for RH=Yes; ESTH-OAH=1' - 5 1/2"; ESTH-OAW=2' - 5 1/4"; Enclosure for LH=No; Enclosure for RH=Yes; Induction for LH=No; Induction for RH=Yes; Inlet Dia=0' - 11 7/8"; Inlet Radius=0' - 5 15/16"; Inlet for LH=No; Inlet for RH=Yes; Power Connect for LH=No; Power Connect for RH=Yes; Q5A=1' - 8"; Q5B=2' - 0"; Q5Q=1' - 8"; QSTE Discharge Offset=0' - 4 1/2"; Sound Elbow for LH=No; Sound Elbow for RH=No
- QSTE-3/4-HP-14L-W/OUT S/ELBOW: BoX H=1' - 8"; Box H=1' - 8"; Box L=4' - 0"; Box W=4' - 0"; DUCT-C=1' - 9"; DUCT-D=1' - 6"; Discharge Height Y=1' - 4"; Discharge Width X=1' - 7"; Discharge for LH=Yes; Discharge for RH=No; ESTH for LH=Yes; ESTH for RH=No; ESTH-OAH=1' - 5 1/2"; ESTH-OAW=2' - 5 1/4"; Enclosure for LH=Yes; Enclosure for RH=No; Induction for LH=Yes; Induction for RH=No; Inlet Dia=1' - 1 7/8"; Inlet Radius=0' - 6 15/16"; Inlet for LH=Yes; Inlet for RH=No; Power Connect for LH=Yes; Power Connect for RH=No; Q5A=1' - 8"; Q5B=2' - 0"; Q5Q=1' - 8"; QSTE Discharge Offset=0' - 4 1/2"; Sound Elbow for LH=No; Sound Elbow for RH=No
- QSTE-3/4-HP-14R-W/OUT S/ELBOW: BoX H=1' - 8"; Box H=1' - 8"; Box L=4' - 0"; Box W=4' - 0"; DUCT-C=1' - 9"; DUCT-D=1' - 6"; Discharge Height Y=1' - 4"; Discharge Width X=1' - 7"; Discharge for LH=No; Discharge for RH=Yes; ESTH for LH=No; ESTH for RH=Yes; ESTH-OAH=1' - 5 1/2"; ESTH-OAW=2' - 5 1/4"; Enclosure for LH=No; Enclosure for RH=Yes; Induction for LH=No; Induction for RH=Yes; Inlet Dia=1' - 1 7/8"; Inlet Radius=0' - 6 15/16"; Inlet for LH=No; Inlet for RH=Yes; Power Connect for LH=No; Power Connect for RH=Yes; Q5A=1' - 8"; Q5B=2' - 0"; Q5Q=1' - 8"; QSTE Discharge Offset=0' - 4 1/2"; Sound Elbow for LH=No; Sound Elbow for RH=No
- QSTE-1/6-HP-8L-S/ELBOW: BoX H=1' - 6"; Box H=1' - 6"; Box L=3' - 0"; Box W=2' - 8"; DUCT-C=1' - 0"; DUCT-D=1' - 4"; Discharge Height Y=0' - 11"; Discharge Width X=0' - 11 1/2"; Discharge for LH=Yes; Discharge for RH=No; ESTH for LH=Yes; ESTH for RH=No; ESTH-OAH=1' - 0 1/2"; ESTH-OAW=1' - 9 3/4"; Enclosure for LH=Yes; Enclosure for RH=No; Induction for LH=No; Induction for RH=No; Inlet Dia=0' - 7 7/8"; Inlet Radius=0' - 3 15/16"; Inlet for LH=Yes; Inlet for RH=No; Power Connect for LH=Yes; Power Connect for RH=No; Q5A=1' - 6"; Q5B=1' - 6"; Q5Q=1' - 6"; QSTE Discharge Offset=0' - 4 1/2"; Sound Elbow for LH=Yes; Sound Elbow for RH=No
- QSTE-1/4-HP-8L-W/OUT S/ELBOW: BoX H=1' - 6"; Box H=1' - 6"; Box L=3' - 0"; Box W=2' - 8"; DUCT-C=1' - 0"; DUCT-D=1' - 4"; Discharge Height Y=0' - 11"; Discharge Width X=0' - 11 1/2"; Discharge for LH=Yes; Discharge for RH=No; ESTH for LH=Yes; ESTH for RH=No; ESTH-OAH=1' - 0 1/2"; ESTH-OAW=1' - 9 3/4"; Enclosure for LH=Yes; Enclosure for RH=No; Induction for LH=Yes; Induction for RH=No; Inlet Dia=0' - 7 7/8"; Inlet Radius=0' - 3 15/16"; Inlet for LH=Yes; Inlet for RH=No; Power Connect for LH=Yes; Power Connect for RH=No; Q5A=1' - 6"; Q5B=1' - 6"; Q5Q=1' - 6"; QSTE Discharge Offset=0' - 4 1/2"; Sound Elbow for LH=No; Sound Elbow for RH=No
- QSTE-1/4-HP-8R-S/ELBOW: BoX H=1' - 6"; Box H=1' - 6"; Box L=3' - 0"; Box W=2' - 8"; DUCT-C=1' - 0"; DUCT-D=1' - 4"; Discharge Height Y=0' - 11"; Discharge Width X=0' - 11 1/2"; Discharge for LH=No; Discharge for RH=Yes; ESTH for LH=No; ESTH for RH=Yes; ESTH-OAH=1' - 0 1/2"; ESTH-OAW=1' - 9 3/4"; Enclosure for LH=No; Enclosure for RH=Yes; Induction for LH=No; Induction for RH=No; Inlet Dia=0' - 7 7/8"; Inlet Radius=0' - 3 15/16"; Inlet for LH=No; Inlet for RH=Yes; Power Connect for LH=No; Power Connect for RH=Yes; Q5A=1' - 6"; Q5B=1' - 6"; Q5Q=1' - 6"; QSTE Discharge Offset=0' - 4 1/2"; Sound Elbow for LH=No; Sound Elbow for RH=Yes
- QSTE-1/4-HP-8R-W/OUT S/ELBOW: BoX H=1' - 6"; Box H=1' - 6"; Box L=3' - 0"; Box W=2' - 8"; DUCT-C=1' - 0"; DUCT-D=1' - 4"; Discharge Height Y=0' - 11"; Discharge Width X=0' - 11 1/2"; Discharge for LH=No; Discharge for RH=Yes; ESTH for LH=No; ESTH for RH=Yes; ESTH-OAH=1' - 0 1/2"; ESTH-OAW=1' - 9 3/4"; Enclosure for LH=No; Enclosure for RH=Yes; Induction for LH=No; Induction for RH=Yes; Inlet Dia=0' - 7 7/8"; Inlet Radius=0' - 3 15/16"; Inlet for LH=No; Inlet for RH=Yes; Power Connect for LH=No; Power Connect for RH=Yes; Q5A=1' - 6"; Q5B=1' - 6"; Q5Q=1' - 6"; QSTE Discharge Offset=0' - 4 1/2"; Sound Elbow for LH=No; Sound Elbow for RH=No
- QSTE-1/2-HP-10L-S/ELBOW: BoX H=1' - 6"; Box H=1' - 6"; Box L=3' - 4"; Box W=3' - 4"; DUCT-C=1' - 5"; DUCT-D=1' - 4"; Discharge Height Y=1' - 0"; Discharge Width X=1' - 2"; Discharge for LH=Yes; Discharge for RH=No; ESTH for LH=Yes; ESTH for RH=No; ESTH-OAH=1' - 1 1/2"; ESTH-OAW=2' - 0 1/4"; Enclosure for LH=Yes; Enclosure for RH=No; Induction for LH=No; Induction for RH=No; Inlet Dia=0' - 9 7/8"; Inlet Radius=0' - 4 15/16"; Inlet for LH=Yes; Inlet for RH=No; Power Connect for LH=Yes; Power Connect for RH=No; Q5A=1' - 6"; Q5B=1' - 8"; Q5Q=1' - 6"; QSTE Discharge Offset=0' - 4 1/2"; Sound Elbow for LH=Yes; Sound Elbow for RH=No

## geometry (parser evidence)
native form markers: Sweep x32
no freeform markers — native parametric forms only
